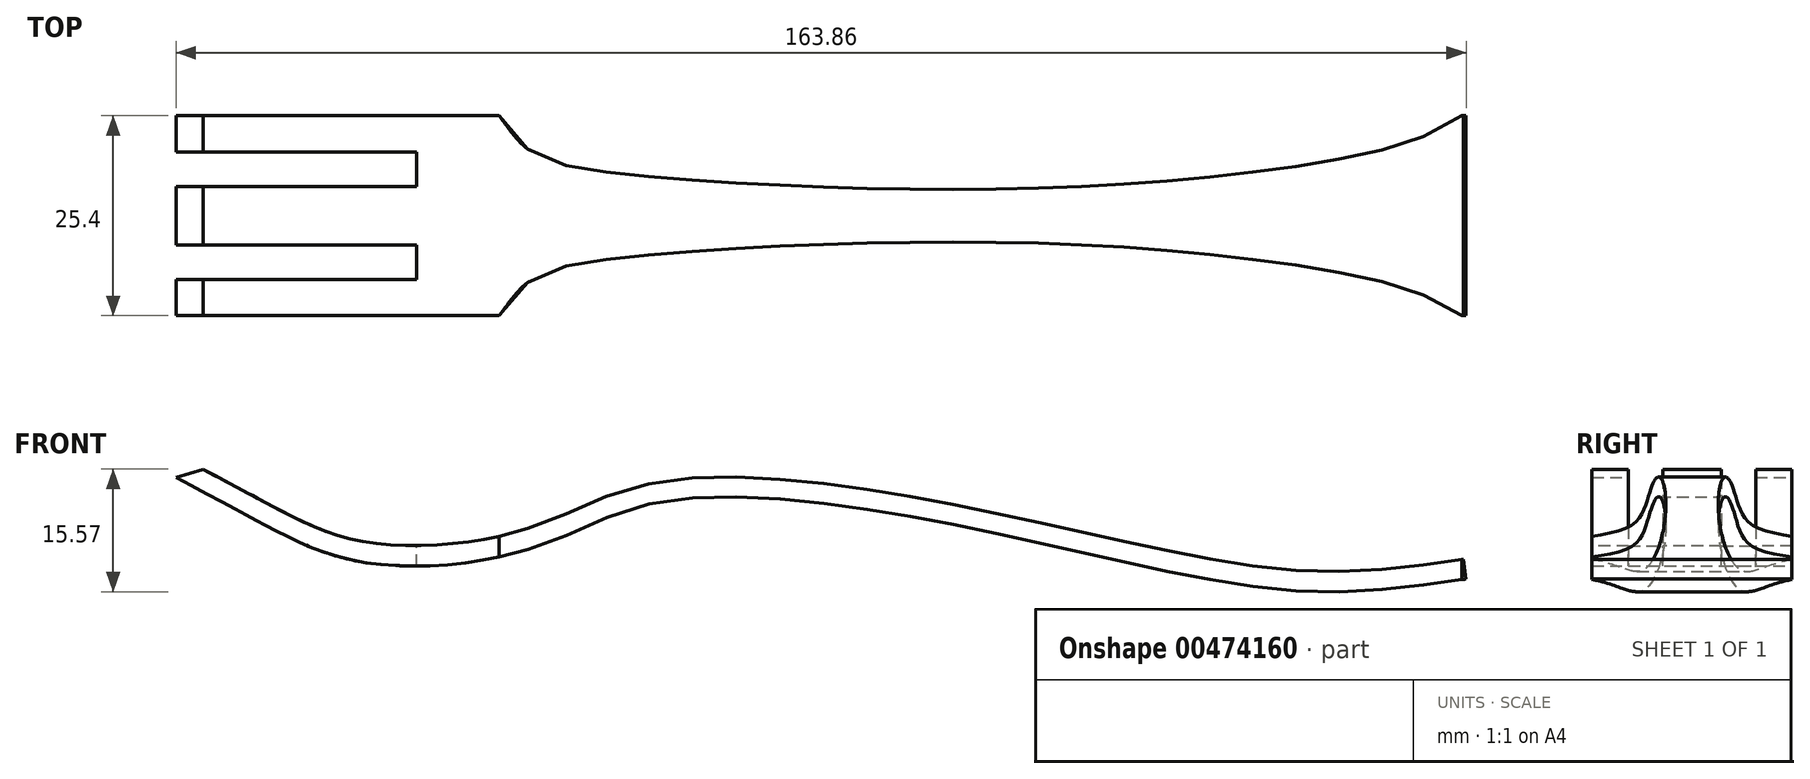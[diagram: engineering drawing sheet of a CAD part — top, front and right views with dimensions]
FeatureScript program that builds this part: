
annotation { "Feature Type Name" : "Feature", "Feature Type Description" : "" }
export const myFeature = defineFeature(function(context is Context, id is Id, definition is map)
    precondition{}
    {
        {
            var Q0;
            Q0=qCreatedBy(makeId("Front.planeOp"),FACE);
            var sketch = newSketch(context, id + "F0", { "sketchPlane" : qUnion([Q0])});
            skFitSpline(sketch, "E0", {"points": [v(0, 0) * mm, v(13.14, -7.06) * mm, v(25.67, -11.76) * mm, v(45.77, -9.93) * mm, v(60.12, -4.45) * mm, v(88.83, -4.97) * mm, v(124.59, -12.28) * mm, v(147.03, -15.41) * mm, v(164.52, -13.85) * mm], "startDerivative": vector(126.53, -68.5) * mm, "endDerivative": vector(149.1, 21.34) * mm});
            skFitSpline(sketch, "E1.0", {"points": [v(-1.2, -2.23) * mm, v(0.1, -2.95) * mm, v(2.75, -4.37) * mm, v(6, -6.13) * mm, v(8.56, -7.5) * mm, v(10.14, -8.34) * mm, v(11.38, -9) * mm, v(12.6, -9.65) * mm, v(14.14, -10.45) * mm, v(16.02, -11.38) * mm, v(17.98, -12.25) * mm, v(20.04, -13.03) * mm, v(22.24, -13.69) * mm, v(24.6, -14.2) * mm, v(27.15, -14.53) * mm, v(29.8, -14.68) * mm, v(33.47, -14.67) * mm, v(37.21, -14.36) * mm, v(40.88, -13.78) * mm, v(43.55, -13.21) * mm, v(45.68, -12.63) * mm, v(47.3, -12.1) * mm, v(48.84, -11.55) * mm, v(50.65, -10.82) * mm, v(52.67, -9.92) * mm, v(54.6, -9.05) * mm, v(56.5, -8.25) * mm, v(58.11, -7.66) * mm, v(59.44, -7.25) * mm, v(60.48, -6.97) * mm, v(61.56, -6.73) * mm, v(63.08, -6.45) * mm, v(65.12, -6.18) * mm, v(67.78, -6) * mm, v(71.54, -5.9) * mm, v(76.63, -6.1) * mm, v(83.16, -6.72) * mm, v(89.95, -7.68) * mm, v(99.14, -9.3) * mm, v(108.35, -11.28) * mm, v(117.17, -13.26) * mm, v(123.48, -14.66) * mm, v(129.4, -15.88) * mm, v(134.97, -16.88) * mm, v(140.3, -17.6) * mm, v(144.6, -17.92) * mm, v(148, -17.97) * mm, v(151.34, -17.9) * mm, v(155.42, -17.6) * mm, v(160.2, -17.03) * mm, v(163.33, -16.58) * mm, v(164.88, -16.36) * mm]});
            skLineSegment(sketch, "E2", {"start": v(164.52, -13.85) * mm, "end": v(164.88, -16.36) * mm});
            skLineSegment(sketch, "E3", {"start": v(-1.2, -2.23) * mm, "end": v(0, 0) * mm});
            skSolve(sketch);
        }
        {
            var Q0;
            Q0=makeQuery(id+"F0.imprint","IMPRINT",FACE,{"disambiguationData":[TD([[makeQuery(id+"F0.imprint","IMPRINT",EDGE,{"derivedFrom":sQuery(id+"F0.wireOp",EDGE,"E0")}),-1.0]])]});
            extrude(context, id + "F1", {"entities" : qUnion([Q0]), "depth" : 25.4 * mm});
        }
        {
            var Q0;
            Q0=qCreatedBy(makeId("Top.planeOp"),FACE);
            var sketch = newSketch(context, id + "F2", { "sketchPlane" : qUnion([Q0])});
            skFitSpline(sketch, "E4", {"points": [v(0, 0) * mm, v(42.07, 0) * mm], "startDerivative": vector(42.07, 0) * mm, "endDerivative": vector(42.07, 0) * mm});
            skFitSpline(sketch, "E5", {"points": [v(42.07, 0) * mm, v(45.83, -4.34) * mm, v(57.66, -7.4) * mm, v(99.8, -9.36) * mm, v(140.14, -6.85) * mm, v(164.31, 0) * mm], "startDerivative": vector(29.94, -40.22) * mm, "endDerivative": vector(66.39, 52.42) * mm});
            skLineSegment(sketch, "E6", {"start": v(0, -12.7) * mm, "end": v(174.85, -12.7) * mm});
            skLineSegment(sketch, "E7", {"start": v(42.07, 0) * mm, "end": v(164.31, 0) * mm});
            skLineSegment(sketch, "E8.MirrorCS", {"start": v(42.07, -25.4) * mm, "end": v(164.31, -25.4) * mm});
            skFitSpline(sketch, "E9.MirrorCS", {"points": [v(42.07, -25.4) * mm, v(45.83, -21.06) * mm, v(57.66, -18) * mm, v(99.8, -16.04) * mm, v(140.14, -18.55) * mm, v(164.31, -25.4) * mm], "startDerivative": vector(29.94, 40.22) * mm, "endDerivative": vector(66.39, -52.42) * mm});
            skFitSpline(sketch, "E10.MirrorCS", {"points": [v(0, -25.4) * mm, v(42.07, -25.4) * mm], "startDerivative": vector(42.07, 0) * mm, "endDerivative": vector(42.07, 0) * mm});
            skSolve(sketch);
        }
        {
            var Q0;
            Q0=makeQuery(id+"F2.imprint","IMPRINT",FACE,{"disambiguationData":[TD([[makeQuery(id+"F2.imprint","IMPRINT",EDGE,{"derivedFrom":sQuery(id+"F2.wireOp",EDGE,"E8.MirrorCS")}),1.0]])]});
            var Q1;
            Q1=makeQuery(id+"F2.imprint","IMPRINT",FACE,{"disambiguationData":[TD([[makeQuery(id+"F2.imprint","IMPRINT",EDGE,{"derivedFrom":sQuery(id+"F2.wireOp",EDGE,"E5")}),1.0]])]});
            extrude(context, id + "F3", {"entities" : qUnion([Q0, Q1]), "operationType" : NewBodyOperationType.REMOVE, "oppositeDirection" : true, "depth" : 25.4 * mm});
        }
        {
            var Q0;
            Q0=qCreatedBy(makeId("Top.planeOp"),FACE);
            var sketch = newSketch(context, id + "F4", { "sketchPlane" : qUnion([Q0])});
            skLineSegment(sketch, "E11", {"start": v(-7.5, -12.7) * mm, "end": v(176.24, -12.7) * mm});
            skLineSegment(sketch, "E12", {"start": v(-7.5, -8.99) * mm, "end": v(31.53, -8.99) * mm});
            skLineSegment(sketch, "E13", {"start": v(31.53, -4.62) * mm, "end": v(-7.5, -4.62) * mm});
            skLineSegment(sketch, "E14", {"start": v(31.53, -8.99) * mm, "end": v(31.53, -4.62) * mm});
            skLineSegment(sketch, "E15", {"start": v(-7.5, -4.62) * mm, "end": v(-7.5, -8.99) * mm});
            skLineSegment(sketch, "E16.MirrorCS", {"start": v(31.53, -16.41) * mm, "end": v(31.53, -20.78) * mm});
            skLineSegment(sketch, "E17.MirrorCS", {"start": v(-7.5, -16.41) * mm, "end": v(31.53, -16.41) * mm});
            skLineSegment(sketch, "E18.MirrorCS", {"start": v(31.53, -20.78) * mm, "end": v(-7.5, -20.78) * mm});
            skLineSegment(sketch, "E19", {"start": v(-7.5, -20.78) * mm, "end": v(-7.5, -16.41) * mm});
            skSolve(sketch);
        }
        {
            var Q0;
            Q0=makeQuery(id+"F4.imprint","IMPRINT",FACE,{"disambiguationData":[TD([[makeQuery(id+"F4.imprint","IMPRINT",EDGE,{"derivedFrom":sQuery(id+"F4.wireOp",EDGE,"E12")}),1.0]])]});
            var Q1;
            Q1=makeQuery(id+"F4.imprint","IMPRINT",FACE,{"disambiguationData":[TD([[makeQuery(id+"F4.imprint","IMPRINT",EDGE,{"derivedFrom":sQuery(id+"F4.wireOp",EDGE,"E16.MirrorCS")}),-1.0]])]});
            extrude(context, id + "F5", {"entities" : qUnion([Q0, Q1]), "operationType" : NewBodyOperationType.REMOVE, "oppositeDirection" : true, "depth" : 25.4 * mm, "hasSecondDirection" : true, "secondDirectionOppositeDirection" : false, "secondDirectionDepth" : 25.4 * mm});
        }
        {
            var Q0;
            {var subQ0=sQuery(id+"F0.wireOp",EDGE,"E0");var subQ1=sQuery(id+"F0.wireOp",EDGE,"E3");Q0=makeQuery(id+"F5.boolean.opBoolean","SPLIT",EDGE,{"disambiguationData":[TD([makeQuery(id+"F5.opExtrude","SWEPT_FACE",FACE,{"disambiguationData":[OSD([sQuery(id+"F4.wireOp",EDGE,"E12")])]})])],"derivedFrom":makeQuery(id+"F1.opExtrude","SWEPT_EDGE",EDGE,{"disambiguationData":[OSD([subQ0,subQ1])]})});}
            var Q1;
            {var subQ0=sQuery(id+"F0.wireOp",EDGE,"E0");var subQ1=sQuery(id+"F0.wireOp",EDGE,"E3");Q1=makeQuery(id+"F5.boolean.opBoolean","SPLIT",EDGE,{"disambiguationData":[TD([makeQuery(id+"F5.opExtrude","SWEPT_FACE",FACE,{"disambiguationData":[OSD([sQuery(id+"F4.wireOp",EDGE,"E13")])]})])],"derivedFrom":makeQuery(id+"F1.opExtrude","SWEPT_EDGE",EDGE,{"disambiguationData":[OSD([subQ0,subQ1])]})});}
            var Q2;
            {var subQ0=sQuery(id+"F0.wireOp",EDGE,"E0");var subQ1=sQuery(id+"F0.wireOp",EDGE,"E3");Q2=makeQuery(id+"F5.boolean.opBoolean","SPLIT",EDGE,{"disambiguationData":[TD([makeQuery(id+"F5.opExtrude","SWEPT_FACE",FACE,{"disambiguationData":[OSD([sQuery(id+"F4.wireOp",EDGE,"E18.MirrorCS")])]})])],"derivedFrom":makeQuery(id+"F1.opExtrude","SWEPT_EDGE",EDGE,{"disambiguationData":[OSD([subQ0,subQ1])]})});}
            chamfer(context, id + "F6", {"entities" : qUnion([Q0, Q1, Q2]), "width" : 5.08 * mm, "tangentPropagation" : true});
        }
    });
